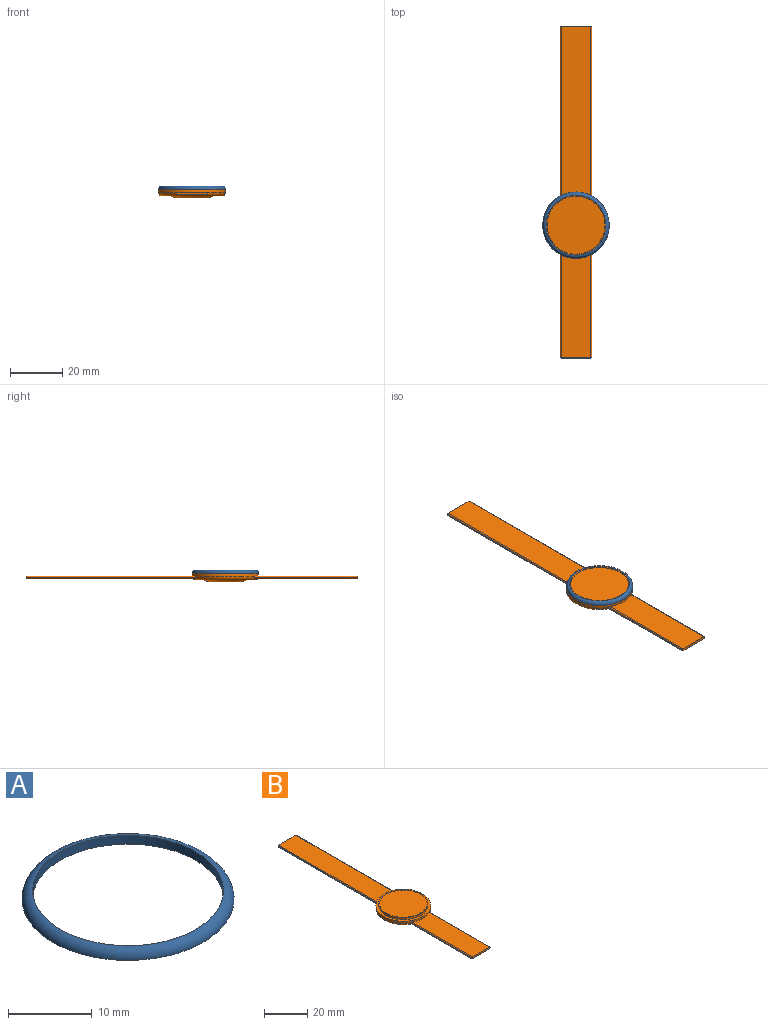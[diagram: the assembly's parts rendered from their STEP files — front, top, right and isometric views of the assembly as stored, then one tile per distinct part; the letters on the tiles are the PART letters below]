
ASSEMBLY  parts=2 mates=1
PART A: 3 faces, bbox 27.5x27.5x1.3 mm
  f0: cylinder r=11.43mm len=22.86mm, axis (0,0,-1), area 91.2mm2, adj f1,f2
  f1: plane 25.4x25.4mm, normal (0,0,-1), area 96.3mm2, adj f0,f2
  f2: torus R=11.43mm, axis (0,0,1), area 153.4mm2, adj f0,f1
PART B: 29 faces, bbox 27.5x127x4.6 mm
  f0: cylinder r=11.11mm len=22.23mm, axis (0,0,-1), area 8.9mm2, adj f25,f28
  f1: cylinder r=11.43mm len=22.86mm, axis (0,0,-1), area 91.2mm2, adj f2,f5
  f2: plane 22.86x22.86mm, normal (0,0,1), area 4.5mm2, adj f1,f28
  f3: plane 22.86x22.86mm, normal (0,0,-1), area 190.3mm2, adj f6,f27
  f4: cylinder r=12.7mm len=25.4mm, axis (0,0,-1), area 95.7mm2, adj f5,f6,f13,f14,f15,f17,f23,f24
  f5: plane 25.4x25.4mm, normal (0,0,1), area 96.3mm2, adj f1,f4
  f6: torus R=11.43mm, axis (0,0,1), area 132.4mm2, adj f3,f4,f8,f9,f10,f11,f12,f13
  f7: plane 12.08x1.01mm, normal (0,-1,0), area 12.1mm2, adj f8,f9,f10,f11,f12,f13,f14,f15
  f8: plane 39.71x0.26mm, normal (1,0,0), area 9.9mm2, adj f6,f7,f10,f14
  f9: plane 39.73x11.32mm, normal (0,0,-1), area 439.4mm2, adj f6,f7,f10,f12
  f10: cylinder r=0.38mm len=39.79mm, axis (0,1,0), area 23.8mm2, adj f6,f7,f8,f9
  f11: plane 39.71x0.26mm, normal (-1,0,0), area 9.9mm2, adj f6,f7,f12,f13
  f12: cylinder r=0.38mm len=39.79mm, axis (0,-1,0), area 23.8mm2, adj f6,f7,f9,f11
  f13: cylinder r=0.38mm len=39.64mm, axis (0,1,0), area 23.7mm2, adj f4,f6,f7,f11,f15
  f14: cylinder r=0.38mm len=39.64mm, axis (0,-1,0), area 23.7mm2, adj f4,f6,f7,f8,f15
  f15: plane 39.43x11.32mm, normal (0,0,1), area 436.2mm2, adj f4,f7,f13,f14
  f16: plane 12.08x1.01mm, normal (0,1,0), area 12.1mm2, adj f17,f18,f19,f20,f21,f22,f23,f24
  f17: plane 64.83x11.32mm, normal (0,0,1), area 723.7mm2, adj f4,f16,f23,f24
  f18: plane 65.13x11.32mm, normal (0,0,-1), area 726.9mm2, adj f6,f16,f19,f20
  f19: cylinder r=0.38mm len=65.19mm, axis (0,-1,0), area 39mm2, adj f6,f16,f18,f21
  f20: cylinder r=0.38mm len=65.19mm, axis (0,1,0), area 39mm2, adj f6,f16,f18,f22
  f21: plane 65.11x0.26mm, normal (-1,0,0), area 16.2mm2, adj f6,f16,f19,f23
  f22: plane 65.11x0.26mm, normal (1,0,0), area 16.2mm2, adj f6,f16,f20,f24
  f23: cylinder r=0.38mm len=65.04mm, axis (0,1,0), area 38.9mm2, adj f4,f6,f16,f17,f21
  f24: cylinder r=0.38mm len=65.04mm, axis (0,-1,0), area 38.9mm2, adj f4,f6,f16,f17,f22
  f25: plane 22.23x22.23mm, normal (0,0,1), area 387.9mm2, adj f0
  f26: plane 10.1x10.1mm, normal (0,0,-1), area 80.1mm2, adj f27
  f27: torus R=5.05mm, axis (0,0,-1), area 145.5mm2, adj f3,f26
  f28: torus R=11.37mm, axis (0,0,1), area 28.1mm2, adj f0,f2
PLACE A t=(0,0,0.36)mm
PLACE B t=(0,0,-2.18)mm
MATE revolute A.f0 <-> B.f0  axis (0,0,1) through (0,0,1.63)mm
